# Revit family: Sirene Audiovisual SAVQW ILUMAC
name_source: partatom
category: Dispositivos de alarme de incêndio
units: mm (PartAtom-declared; Revit-internal decimal feet)

## family parameters
Com base no plano de trabalho = Não
Compartilhado = Não
Corte com vazios quando carregada = Não
Cota do conector redondo = Utilizar diâmetro
Manter orientação da anotação = Não
Número OmniClass = 23.75.00.00
Ponto de cálculo do ambiente = Não
Sempre na vertical = Sim
Tipo de parte = Normal
Título OmniClass = Climate Control (HVAC)

## types (5) — shared parameters
Dimensões (AxLxP) = 122x122x80mm
Fabricante = ILUMAC
Fixação = Sobrepor com furação para rosca 3/4” BSP
Grau de proteção = IP65 (uso externo)
Material da caixa = Plástico ABS vermelho com proteção UV
Normas técnicas aplicáveis = ABNT NBR 17240:2010 | ABNT NBR ISO 7240-3
Tensão nominal = 24Vcc
Umidade relativa = 0 a 95% (sem condensação)
zero-valued in all types: Elevação padrão

## per-type parameters (varying)
| type | Alimentação externa | Consumo | Consumo da fonte auxiliar ou V+ | Código do Produto | Descrição | Endereços programáveis | Endereços utilizados | Peso | Protocolo de comunicação | Sinalização Sonora | Sinalização Visual | Temperatura de operação | Tensão de operação | Topologia de ligação |
| SAVQW-C |  |  |  | 002055 | Sirene Audiovisual Convencional IP65 SAVQW-C |  |  | 230g |  | 96dB @ 1m – bitonal | 12 leds / Pisca na cor vermelha | -5 a +55oC | 20 a 28Vcc | 2 fios (com polaridade) |
| SAVQW-E |  |  |  | 002257 | Sirene Audiovisual Endereçável IP65 SAVQW-E | 001 a 500 |  | 230g | ALF-500 (proprietário) | 96dB @ 1m – bitonal | 12 leds / Pisca na cor vermelha | -5 a +55oC | 22 a 28Vcc | Classe A e Classe B (3 fios) |
| SAVQW-D | V+ ou Fonte 22 a 28Vcc (não acompanha o dispositivo) | 350uA em supervisão (rede endereçável)
3mA em alarme (rede endereçável)
15mA @ 28Vcc em alarme (alimentação externa ou V+) |  | 0040046 | Sirene Audiovisual Endereçável Sirius IP65 SAVQW-D | Sirius l = 106 a 125 / Sirius ll = 001 a 125 |  | 250g | ALF-1000-2 (proprietário) | 103dB @ 1m – bitonal | Pisca na cor vermelha | -5 a +55oC | 22 a 30Vcc | a Classe A e Classe B (2 fios) |
| SAVQW-D (Comp. Sirius 1) | V+ ou Fonte 22 a 28Vcc (não acompanha o dispositivo) | 350uA em supervisão (rede endereçável)
3mA em alarme (rede endereçável)
15mA @ 28Vcc em alarme (alimentação externa ou V+) |  | 0040068 | Sirene Audiovisual Endereçável Sirius IP65 SAVQW-D (Comp. Sirius 1) | Sirius l = 106 a 125 / Sirius ll = 001 a 125 |  | 250g | ALF-1000-2 (proprietário) | 103dB @ 1m – bitonal | Pisca na cor vermelha | -5 a +55oC | 22 a 30Vcc | a Classe A e Classe B (2 fios) |
| SAVQW-G | V+ ou Fonte 22 a 28Vcc (não acompanha o dispositivo) | 350uA em supervisão / 3mA em alarme
3mA em alarme (rede endereçável)
15mA @ 28Vcc em alarme (alimentação externa ou V+) | 15mA @ 28Vcc em alarme | 007029 | Sirene Audiovisual Endereçável Cygnus IP65 SAVQW-G | 001 a 125 (por laço) | 1 endereço | 250g | CYGNUS (proprietário) | 96dB @ 1m – bitonal | Pisca na cor vermelha | -5ºC a +55oC | 20 a 30Vcc | a Classe A e Classe B (2 fios) |

note: column(s) folded — value = type name in every type: Modelo
